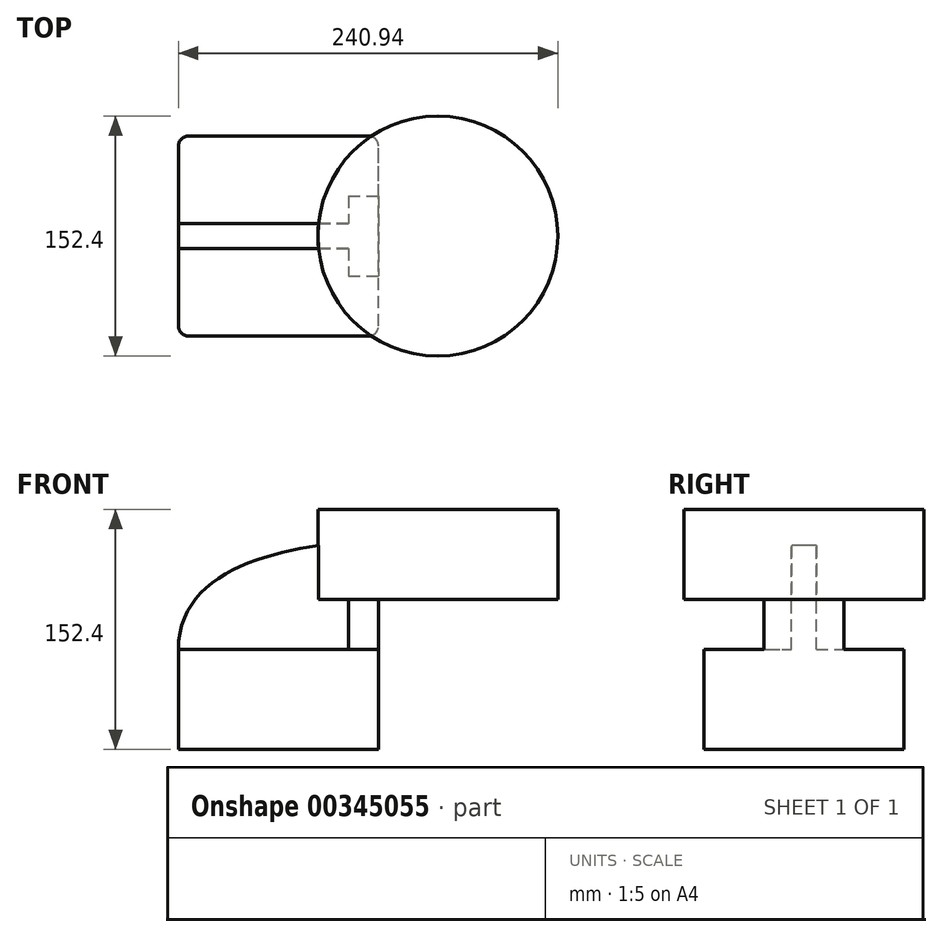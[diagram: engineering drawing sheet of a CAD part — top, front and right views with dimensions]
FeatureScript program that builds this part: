
annotation { "Feature Type Name" : "Feature", "Feature Type Description" : "" }
export const myFeature = defineFeature(function(context is Context, id is Id, definition is map)
    precondition{}
    {
        {
            var Q0;
            Q0=qCreatedBy(makeId("Front.planeOp"),FACE);
            var sketch = newSketch(context, id + "F0", { "sketchPlane" : qUnion([Q0])});
            skLineSegment(sketch, "E0.bottom", {"start": v(0, 0) * mm, "end": v(-127, 0) * mm});
            skLineSegment(sketch, "E0.top", {"start": v(0, 63.5) * mm, "end": v(-127, 63.5) * mm});
            skLineSegment(sketch, "E0.left", {"start": v(0, 0) * mm, "end": v(0, 63.5) * mm});
            skLineSegment(sketch, "E0.right", {"start": v(-127, 0) * mm, "end": v(-127, 63.5) * mm});
            skLineSegment(sketch, "E1.bottom", {"start": v(37.74, 95.25) * mm, "end": v(113.94, 95.25) * mm});
            skLineSegment(sketch, "E1.top", {"start": v(37.74, 152.4) * mm, "end": v(113.94, 152.4) * mm});
            skLineSegment(sketch, "E1.left", {"start": v(37.74, 95.25) * mm, "end": v(37.74, 152.4) * mm});
            skLineSegment(sketch, "E1.right", {"start": v(113.94, 95.25) * mm, "end": v(113.94, 152.4) * mm});
            skLineSegment(sketch, "E2", {"start": v(0, 63.5) * mm, "end": v(0, 98.43) * mm});
            skArc(sketch, "E3", {"start": v(0, 98.43) * mm, "mid": v(4.65, 109.65) * mm, "end": v(15.87, 114.3) * mm});
            skLineSegment(sketch, "E4", {"start": v(15.87, 114.3) * mm, "end": v(57.74, 114.3) * mm});
            skLineSegment(sketch, "E5.0", {"start": v(15.87, 133.35) * mm, "end": v(57.74, 133.35) * mm});
            skArc(sketch, "E5.1", {"start": v(-19.05, 98.43) * mm, "mid": v(-8.82, 123.12) * mm, "end": v(15.87, 133.35) * mm});
            skLineSegment(sketch, "E5.2", {"start": v(-19.05, 63.5) * mm, "end": v(-19.05, 98.43) * mm});
            skLineSegment(sketch, "E6", {"start": v(57.74, 114.3) * mm, "end": v(57.74, 133.35) * mm});
            skLineSegment(sketch, "E7", {"start": v(0, 63.5) * mm, "end": v(-19.05, 63.5) * mm});
            skFitSpline(sketch, "E8", {"points": [v(-127, 63.5) * mm, v(15.87, 133.35) * mm], "startDerivative": vector(-0.83, 182.55) * mm, "endDerivative": vector(157.43, 1.52) * mm});
            skSolve(sketch);
        }
        {
            var Q0;
            Q0=makeQuery(id+"F0.imprint","IMPRINT",FACE,{"disambiguationData":[TD([[makeQuery(id+"F0.imprint","IMPRINT",EDGE,{"derivedFrom":sQuery(id+"F0.wireOp",EDGE,"E0.bottom")}),-1.0]])]});
            extrude(context, id + "F1", {"entities" : qUnion([Q0]), "endBound" : BoundingType.SYMMETRIC, "depth" : 127 * mm});
        }
        {
            var Q0;
            Q0=makeQuery(id+"F0.imprint","IMPRINT",FACE,{"disambiguationData":[TD([[makeQuery(id+"F0.imprint","IMPRINT",EDGE,{"derivedFrom":sQuery(id+"F0.wireOp",EDGE,"E2")}),1.0]])]});
            var Q1;
            {var subQ5=sQuery(id+"F0.wireOp",EDGE,"E6");Q1=makeQuery(id+"F0.imprint","IMPRINT",FACE,{"disambiguationData":[TD([[makeQuery(id+"F0.imprint","IMPRINT",EDGE,{"derivedFrom":subQ5}),1.0]])]});}
            extrude(context, id + "F2", {"entities" : qUnion([Q0, Q1]), "operationType" : NewBodyOperationType.ADD, "endBound" : BoundingType.SYMMETRIC, "depth" : 50.8 * mm});
        }
        {
            var Q0;
            {var subQ0=sQuery(id+"F0.wireOp",EDGE,"E0.top");Q0=makeQuery(id+"F0.imprint","IMPRINT",FACE,{"disambiguationData":[TD([[makeQuery(id+"F0.imprint","IMPRINT",EDGE,{"derivedFrom":subQ0}),-1.0]])]});}
            extrude(context, id + "F3", {"entities" : qUnion([Q0]), "operationType" : NewBodyOperationType.ADD, "endBound" : BoundingType.SYMMETRIC, "depth" : 15.88 * mm});
        }
        {
            var Q0;
            {var subQ5=sQuery(id+"F0.wireOp",EDGE,"E1.bottom");Q0=makeQuery(id+"F0.imprint","IMPRINT",FACE,{"disambiguationData":[TD([[makeQuery(id+"F0.imprint","IMPRINT",EDGE,{"derivedFrom":subQ5}),1.0]])]});}
            var Q1;
            Q1=sQuery(id+"F0.wireOp",EDGE,"E1.left");
            revolve(context, id + "F4", {"operationType" : NewBodyOperationType.ADD, "entities" : qUnion([Q0]), "axis" : qUnion([Q1]), "revolveType" : RevolveType.FULL});
        }
        {
            var Q0;
            Q0=makeQuery(id+"F1.opExtrude","CAP_EDGE",EDGE,{"disambiguationData":[OSD([sQuery(id+"F0.wireOp",EDGE,"E0.right")])],"isStart":false});
            var Q1;
            Q1=makeQuery(id+"F1.opExtrude","CAP_EDGE",EDGE,{"disambiguationData":[OSD([sQuery(id+"F0.wireOp",EDGE,"E0.left")])],"isStart":false});
            var Q2;
            Q2=makeQuery(id+"F1.opExtrude","CAP_EDGE",EDGE,{"disambiguationData":[OSD([sQuery(id+"F0.wireOp",EDGE,"E0.right")])],"isStart":true});
            var Q3;
            Q3=makeQuery(id+"F1.opExtrude","CAP_EDGE",EDGE,{"disambiguationData":[OSD([sQuery(id+"F0.wireOp",EDGE,"E0.left")])],"isStart":true});
            fillet(context, id + "F5", {"entities" : qUnion([Q0, Q1, Q2, Q3]), "radius" : 6.35 * mm, "tangentPropagation" : true, "allowEdgeOverflow" : false});
        }
    });
